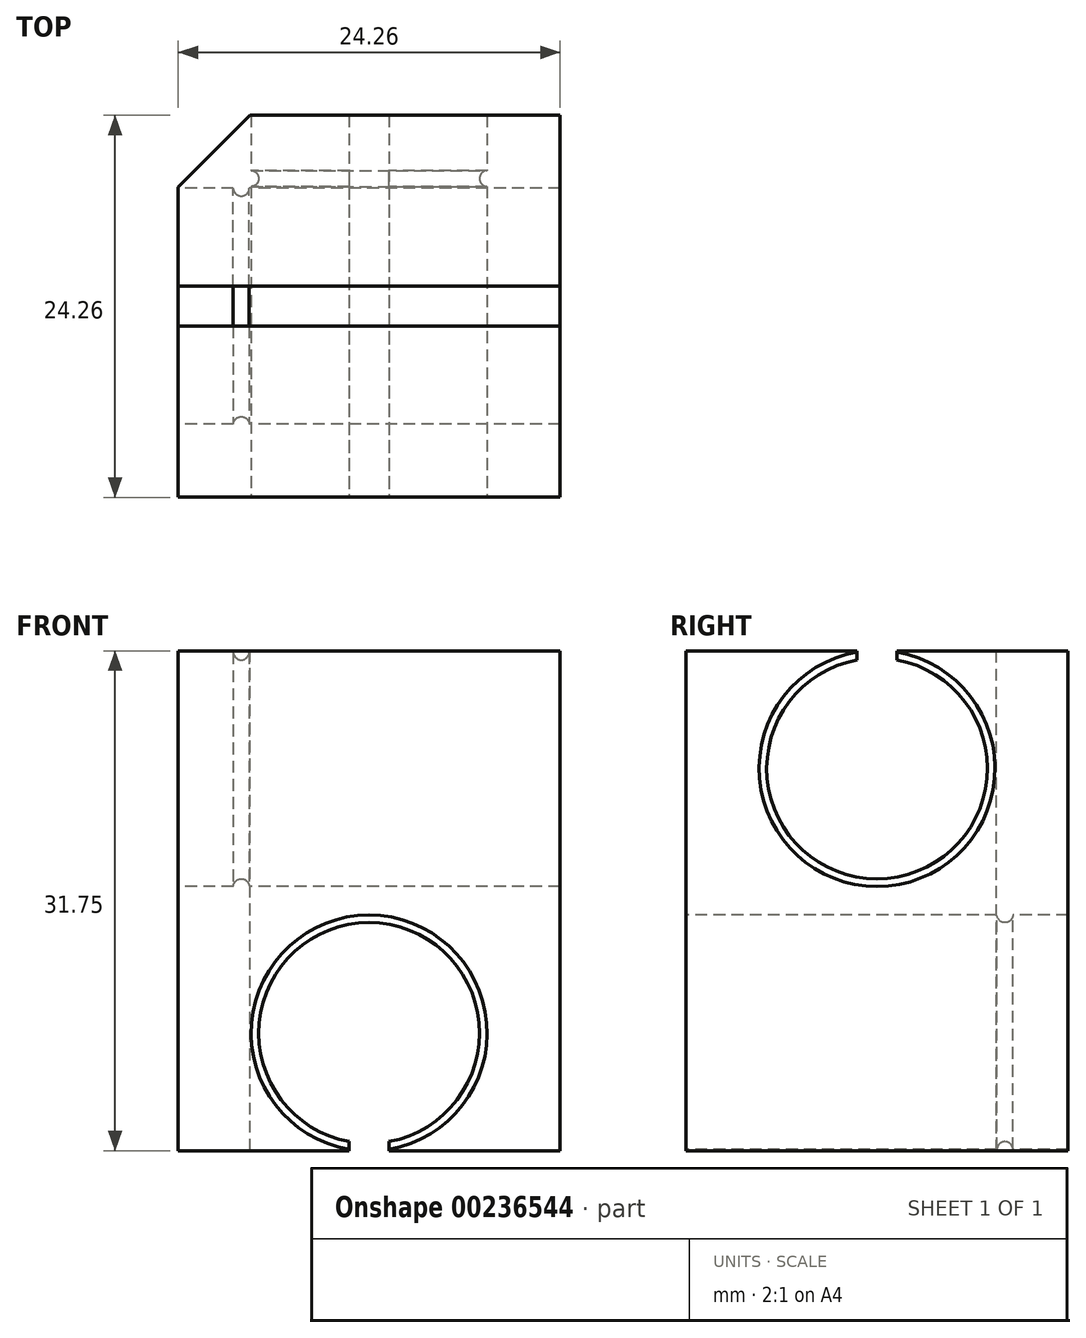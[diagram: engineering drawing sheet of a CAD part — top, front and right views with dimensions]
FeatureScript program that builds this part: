
annotation { "Feature Type Name" : "Feature", "Feature Type Description" : "" }
export const myFeature = defineFeature(function(context is Context, id is Id, definition is map)
    precondition{}
    {
        {
            var Q0;
            Q0=qCreatedBy(makeId("Top.planeOp"),FACE);
            var sketch = newSketch(context, id + "F0", { "sketchPlane" : qUnion([Q0])});
            skLineSegment(sketch, "E0.bottom", {"start": v(12.13, 12.13) * mm, "end": v(-12.13, 12.13) * mm});
            skLineSegment(sketch, "E0.top", {"start": v(12.13, -12.13) * mm, "end": v(-12.13, -12.13) * mm});
            skLineSegment(sketch, "E0.left", {"start": v(12.13, 12.13) * mm, "end": v(12.13, -12.13) * mm});
            skLineSegment(sketch, "E0.right", {"start": v(-12.13, 12.13) * mm, "end": v(-12.13, -12.13) * mm});
            skPoint(sketch, "E0.middle", {"position": v(0, 0) * mm});
            skSolve(sketch);
        }
        {
            var Q0;
            Q0=makeQuery(id+"F0.imprint","IMPRINT",FACE,{"disambiguationData":[TD([[makeQuery(id+"F0.imprint","IMPRINT",EDGE,{"derivedFrom":sQuery(id+"F0.wireOp",EDGE,"E0.bottom")}),1.0]])]});
            extrude(context, id + "F1", {"entities" : qUnion([Q0]), "depth" : 31.75 * mm});
        }
        {
            var Q0;
            Q0=makeQuery(id+"F1.opExtrude","SWEPT_FACE",FACE,{"disambiguationData":[OSD([sQuery(id+"F0.wireOp",EDGE,"E0.top")])]});
            var sketch = newSketch(context, id + "F2", { "sketchPlane" : qUnion([Q0])});
            skArc(sketch, "E1", {"start": v(1.27, 0.09) * mm, "mid": v(0, 14.97) * mm, "end": v(-1.27, 0.09) * mm});
            skLineSegment(sketch, "E2", {"start": v(-1.27, 0.09) * mm, "end": v(-1.27, 0) * mm});
            skLineSegment(sketch, "E3", {"start": v(-1.27, 0) * mm, "end": v(1.27, 0) * mm});
            skLineSegment(sketch, "E4", {"start": v(1.27, 0) * mm, "end": v(1.27, 0.09) * mm});
            skLineSegment(sketch, "E5", {"start": v(1.27, 0.09) * mm, "end": v(-1.27, 0.09) * mm, "construction": true});
            skLineSegment(sketch, "E6", {"start": v(0, 0.09) * mm, "end": v(0, 7.47) * mm, "construction": true});
            skSolve(sketch);
        }
        {
            var Q0;
            Q0 = qSketchRegion(id + "F2", true);
            extrude(context, id + "F3", {"entities" : qUnion([Q0]), "operationType" : NewBodyOperationType.REMOVE, "oppositeDirection" : true, "depth" : 25.4 * mm});
        }
        {
            var Q0;
            Q0=makeQuery(id+"F1.opExtrude","SWEPT_FACE",FACE,{"disambiguationData":[OSD([sQuery(id+"F0.wireOp",EDGE,"E0.right")])]});
            var sketch = newSketch(context, id + "F4", { "sketchPlane" : qUnion([Q0])});
            skCircle(sketch, "E7", {"center": v(0, 24.28) * mm, "radius": 7.5 * mm});
            skPoint(sketch, "E8", {"position": v(0, 31.75) * mm});
            skLineSegment(sketch, "E9", {"start": v(1.27, 31.66) * mm, "end": v(1.27, 31.75) * mm});
            skLineSegment(sketch, "E10", {"start": v(1.27, 31.75) * mm, "end": v(-1.27, 31.75) * mm});
            skLineSegment(sketch, "E11", {"start": v(-1.27, 31.75) * mm, "end": v(-1.27, 31.66) * mm});
            skLineSegment(sketch, "E12", {"start": v(-1.27, 31.66) * mm, "end": v(1.27, 31.66) * mm, "construction": true});
            skLineSegment(sketch, "E13", {"start": v(0, 24.28) * mm, "end": v(0, 31.66) * mm, "construction": true});
            skSolve(sketch);
        }
        {
            var Q0;
            Q0 = qSketchRegion(id + "F4", true);
            extrude(context, id + "F5", {"entities" : qUnion([Q0]), "operationType" : NewBodyOperationType.REMOVE, "oppositeDirection" : true, "depth" : 25.4 * mm});
        }
        {
            var Q0;
            Q0=makeQuery(id+"F1.opExtrude","SWEPT_FACE",FACE,{"disambiguationData":[OSD([sQuery(id+"F0.wireOp",EDGE,"E0.right")])]});
            cPlane(context, id + "F6", {"entities" : qUnion([Q0]), "cplaneType" : CPlaneType.OFFSET, "offset" : 3.5 * mm, "oppositeDirection" : true, "width" : 152.4 * mm, "height" : 152.4 * mm});
        }
        {
            var Q0;
            Q0=makeQuery(id+"F1.opExtrude","SWEPT_FACE",FACE,{"disambiguationData":[OSD([sQuery(id+"F0.wireOp",EDGE,"E0.bottom")])]});
            cPlane(context, id + "F7", {"entities" : qUnion([Q0]), "cplaneType" : CPlaneType.OFFSET, "offset" : 3.5 * mm, "oppositeDirection" : true, "width" : 152.4 * mm, "height" : 152.4 * mm});
        }
        {
            var Q0;
            Q0=qCreatedBy(id+"F6.planeOp",FACE);
            var sketch = newSketch(context, id + "F8", { "sketchPlane" : qUnion([Q0])});
            skArc(sketch, "E14.0", {"start": v(-1.27, 31.66) * mm, "mid": v(0, 16.78) * mm, "end": v(1.27, 31.66) * mm});
            skArc(sketch, "E15", {"start": v(-1.27, 31.17) * mm, "mid": v(0, 17.27) * mm, "end": v(1.27, 31.17) * mm});
            skLineSegment(sketch, "E16", {"start": v(-1.27, 31.66) * mm, "end": v(-1.27, 31.17) * mm});
            skLineSegment(sketch, "E17", {"start": v(1.27, 31.66) * mm, "end": v(1.27, 31.17) * mm});
            skSolve(sketch);
        }
        {
            var Q0;
            Q0 = qSketchRegion(id + "F8", true);
            extrude(context, id + "F9", {"entities" : qUnion([Q0]), "operationType" : NewBodyOperationType.ADD, "oppositeDirection" : true, "depth" : 1.02 * mm});
        }
        {
            var Q0;
            Q0=qCreatedBy(id+"F7.planeOp",FACE);
            var sketch = newSketch(context, id + "F10", { "sketchPlane" : qUnion([Q0])});
            skArc(sketch, "E18.0", {"start": v(-1.27, 0.09) * mm, "mid": v(0, 14.97) * mm, "end": v(1.27, 0.09) * mm});
            skArc(sketch, "E19", {"start": v(1.27, 0.58) * mm, "mid": v(0, 14.48) * mm, "end": v(-1.27, 0.58) * mm});
            skLineSegment(sketch, "E20", {"start": v(-1.27, 0.09) * mm, "end": v(-1.27, 0.58) * mm});
            skLineSegment(sketch, "E21", {"start": v(1.27, 0.09) * mm, "end": v(1.27, 0.58) * mm});
            skSolve(sketch);
        }
        {
            var Q0;
            Q0 = qSketchRegion(id + "F10", true);
            extrude(context, id + "F11", {"entities" : qUnion([Q0]), "operationType" : NewBodyOperationType.ADD, "oppositeDirection" : true, "depth" : 1.02 * mm});
        }
        {
            var Q0;
            Q0=makeQuery(id+"F11.opExtrude","CAP_EDGE",EDGE,{"disambiguationData":[OSD([sQuery(id+"F10.wireOp",EDGE,"E19")])],"isStart":true});
            var Q1;
            Q1=makeQuery(id+"F11.opExtrude","CAP_EDGE",EDGE,{"disambiguationData":[OSD([sQuery(id+"F10.wireOp",EDGE,"E19")])],"isStart":false});
            var Q2;
            Q2=makeQuery(id+"F9.opExtrude","CAP_EDGE",EDGE,{"disambiguationData":[OSD([sQuery(id+"F8.wireOp",EDGE,"E15")])],"isStart":false});
            var Q3;
            Q3=makeQuery(id+"F9.opExtrude","CAP_EDGE",EDGE,{"disambiguationData":[OSD([sQuery(id+"F8.wireOp",EDGE,"E15")])],"isStart":true});
            fillet(context, id + "F12", {"entities" : qUnion([Q0, Q1, Q2, Q3]), "radius" : 0.5 * mm, "tangentPropagation" : true, "allowEdgeOverflow" : false});
        }
        {
            var Q0;
            Q0=makeQuery(id+"F1.opExtrude","SWEPT_EDGE",EDGE,{"disambiguationData":[OSD([sQuery(id+"F0.wireOp",EDGE,"E0.bottom"),sQuery(id+"F0.wireOp",EDGE,"E0.right")])]});
            chamfer(context, id + "F13", {"entities" : qUnion([Q0]), "width" : 4.57 * mm, "tangentPropagation" : true});
        }
    });
